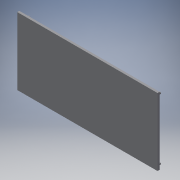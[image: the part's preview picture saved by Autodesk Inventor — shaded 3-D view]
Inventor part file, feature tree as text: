
AUTODESK INVENTOR PART (.ipt)
format: ipt  version: 2017 (Build 210142000, 142)  size: 666,112 bytes
history: native  units: in
note: dims shown in document units (in); Inventor stores cm internally (conversion verified against a paired STEP export)
features: extrude x5, sketch x5, fillet x1
ambient origin geometry x8: Origin, YZ Plane, XZ Plane, XY Plane, X Axis, Y Axis, Z Axis, Center Point
bodies: Solid1 (feature_tree)
feature tree (11):
  extrude  "Extrusion1"  Depth=2.5197in
  extrude  "Extrusion2"  Depth=0.0787in
  extrude  "Extrusion3"  Depth=1.1811in
  extrude  "Extrusion4"  Depth=0.1181in TaperAngle=0.0deg
  extrude  "Extrusion5"  Depth=0.0787in
  fillet  "Fillet1"  Radius=0.0787in
  sketch  "Sketch1"  dims[d0=5.2362in d1=2.5197in]
  sketch  "Sketch2"  dims[d2=0.0787in d3=0.0in d6=1.1811in]
  sketch  "Sketch3"  dims[d7=0.1181in d12=1.1811in]
  sketch  "Sketch4"  dims[d13=0.1378in d14=0.1181in d15=0.0in]
  sketch  "Sketch5"  dims[d19=0.0984in d22=0.0984in d25=0.0787in d29=0.0709in d30=0.1181in d31=0.0in d37=2.5591in d38=1.7717in d39=0.0787in d40=0.0in d41=0.0787in d42=0.0in d43=0.0787in]
